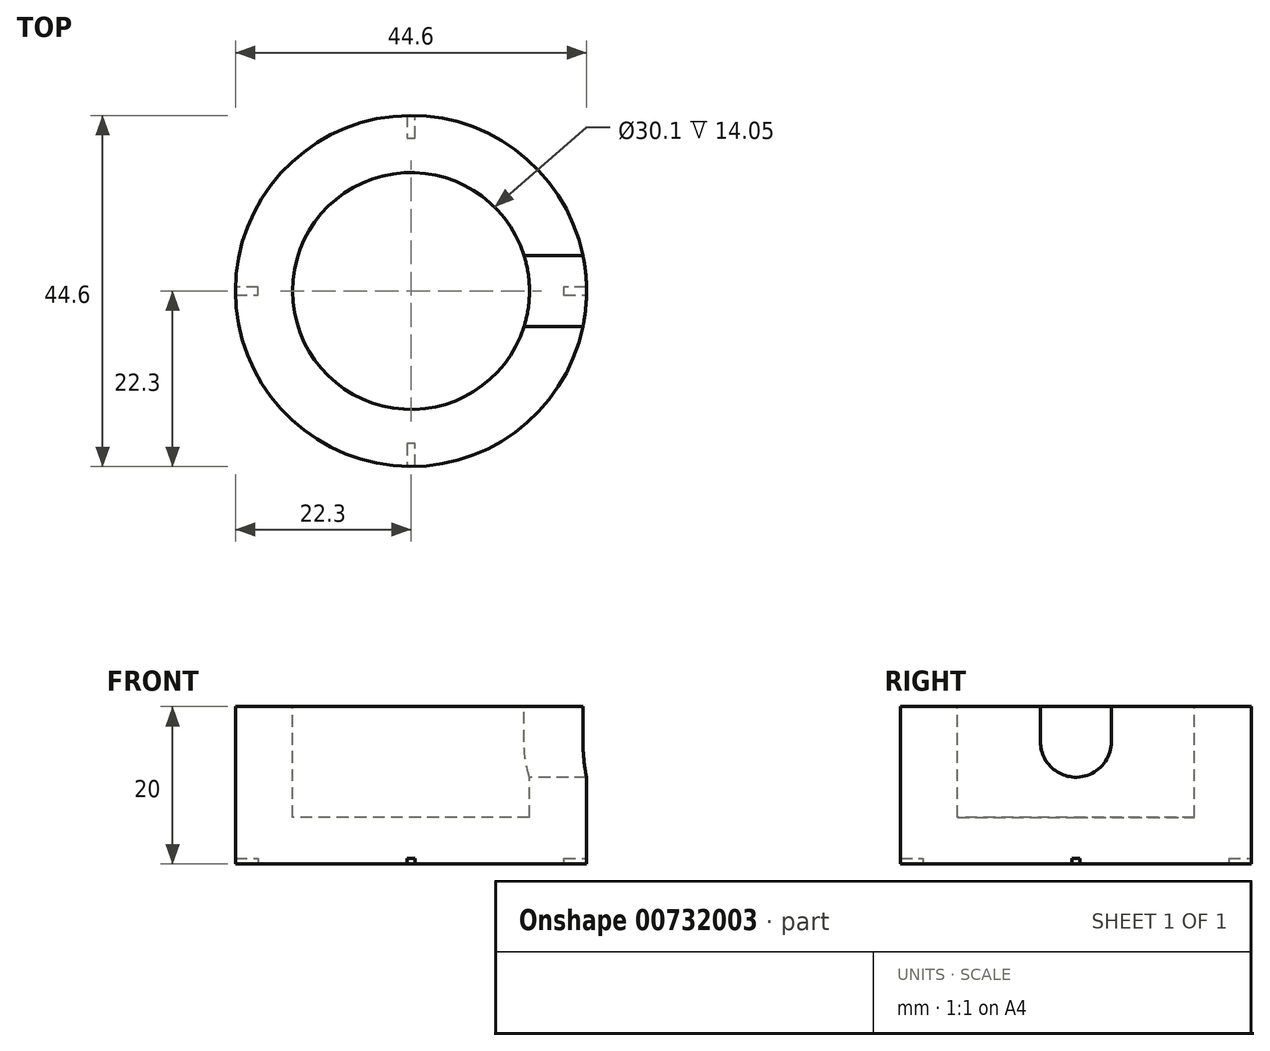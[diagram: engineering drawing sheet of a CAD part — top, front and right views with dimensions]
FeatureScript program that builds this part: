
annotation { "Feature Type Name" : "Feature", "Feature Type Description" : "" }
export const myFeature = defineFeature(function(context is Context, id is Id, definition is map)
    precondition{}
    {
        {
            var Q0;
            Q0=qCreatedBy(makeId("Front.planeOp"),FACE);
            var sketch = newSketch(context, id + "F0", { "sketchPlane" : qUnion([Q0])});
            skLineSegment(sketch, "E0", {"start": v(0, 0) * mm, "end": v(22.3, 0) * mm});
            skLineSegment(sketch, "E1", {"start": v(22.3, 0) * mm, "end": v(22.3, 20) * mm});
            skLineSegment(sketch, "E2", {"start": v(22.3, 20) * mm, "end": v(15.05, 20) * mm});
            skLineSegment(sketch, "E3", {"start": v(15.05, 20) * mm, "end": v(15.05, 5.95) * mm});
            skLineSegment(sketch, "E4", {"start": v(15.05, 5.95) * mm, "end": v(0, 5.95) * mm});
            skLineSegment(sketch, "E5", {"start": v(0, 5.95) * mm, "end": v(0, 0) * mm});
            skSolve(sketch);
        }
        {
            var Q0;
            Q0 = qSketchRegion(id + "F0", true);
            var Q1;
            Q1=sQuery(id+"F0.wireOp",EDGE,"E5");
            revolve(context, id + "F1", {"surfaceOperationType" : NewSurfaceOperationType.NEW, "entities" : qUnion([Q0]), "axis" : qUnion([Q1]), "revolveType" : RevolveType.FULL});
        }
        {
            var Q0;
            Q0=qCreatedBy(makeId("Right.planeOp"),FACE);
            var sketch = newSketch(context, id + "F2", { "sketchPlane" : qUnion([Q0])});
            skLineSegment(sketch, "E6", {"start": v(0, 20.02) * mm, "end": v(4.5, 20.02) * mm});
            skLineSegment(sketch, "E7", {"start": v(4.5, 20.02) * mm, "end": v(4.5, 15.52) * mm});
            skLineSegment(sketch, "E8", {"start": v(-4.5, 15.52) * mm, "end": v(-4.5, 20.02) * mm});
            skLineSegment(sketch, "E9", {"start": v(-4.5, 20.02) * mm, "end": v(0, 20.02) * mm});
            skArc(sketch, "E10", {"start": v(0, 11.04) * mm, "mid": v(-3.18, 12.35) * mm, "end": v(-4.5, 15.54) * mm});
            skPoint(sketch, "E10.startSnap0", {"position": v(0, 15.52) * mm});
            skArc(sketch, "E11", {"start": v(0, 11.04) * mm, "mid": v(3.18, 12.35) * mm, "end": v(4.5, 15.54) * mm});
            skSolve(sketch);
        }
        {
            var Q0;
            Q0=makeQuery(id+"F2.imprint","IMPRINT",FACE,{"disambiguationData":[TD([[makeQuery(id+"F2.imprint","IMPRINT",EDGE,{"derivedFrom":sQuery(id+"F2.wireOp",EDGE,"E6")}),-1.0]])]});
            extrude(context, id + "F3", {"entities" : qUnion([Q0]), "operationType" : NewBodyOperationType.REMOVE, "depth" : 25 * mm, "offsetDistance" : 25 * mm});
        }
        {
            var Q0;
            Q0=qCreatedBy(makeId("Top.planeOp"),FACE);
            var sketch = newSketch(context, id + "F4", { "sketchPlane" : qUnion([Q0])});
            skLineSegment(sketch, "E12", {"start": v(0, -19.4) * mm, "end": v(0.5, -19.4) * mm});
            skLineSegment(sketch, "E13", {"start": v(0.5, -19.4) * mm, "end": v(0.5, -22.4) * mm});
            skLineSegment(sketch, "E14", {"start": v(0.5, -22.4) * mm, "end": v(-0.5, -22.4) * mm});
            skLineSegment(sketch, "E15", {"start": v(-0.5, -22.4) * mm, "end": v(-0.5, -19.4) * mm});
            skLineSegment(sketch, "E16", {"start": v(-0.5, -19.4) * mm, "end": v(0, -19.4) * mm});
            skLineSegment(sketch, "E17", {"start": v(0, 22.42) * mm, "end": v(0.5, 22.42) * mm});
            skLineSegment(sketch, "E18", {"start": v(0.5, 22.42) * mm, "end": v(0.5, 19.42) * mm});
            skLineSegment(sketch, "E19", {"start": v(0.5, 19.42) * mm, "end": v(-0.5, 19.42) * mm});
            skLineSegment(sketch, "E20", {"start": v(-0.5, 19.42) * mm, "end": v(-0.5, 22.42) * mm});
            skLineSegment(sketch, "E21", {"start": v(-0.5, 22.42) * mm, "end": v(0, 22.42) * mm});
            skLineSegment(sketch, "E22", {"start": v(22.4, 0) * mm, "end": v(22.4, -0.5) * mm});
            skLineSegment(sketch, "E23", {"start": v(22.4, -0.5) * mm, "end": v(19.4, -0.5) * mm});
            skLineSegment(sketch, "E24", {"start": v(19.4, -0.5) * mm, "end": v(19.4, 0.5) * mm});
            skLineSegment(sketch, "E25", {"start": v(19.4, 0.5) * mm, "end": v(22.4, 0.5) * mm});
            skLineSegment(sketch, "E26", {"start": v(22.4, 0.5) * mm, "end": v(22.4, 0) * mm});
            skLineSegment(sketch, "E27", {"start": v(-19.4, 0) * mm, "end": v(-19.4, -0.5) * mm});
            skLineSegment(sketch, "E28", {"start": v(-19.4, -0.5) * mm, "end": v(-22.4, -0.5) * mm});
            skLineSegment(sketch, "E29", {"start": v(-22.4, -0.5) * mm, "end": v(-22.4, 0.5) * mm});
            skLineSegment(sketch, "E30", {"start": v(-22.4, 0.5) * mm, "end": v(-19.4, 0.5) * mm});
            skLineSegment(sketch, "E31", {"start": v(-19.4, 0.5) * mm, "end": v(-19.4, 0) * mm});
            skSolve(sketch);
        }
        {
            var Q0;
            Q0 = qSketchRegion(id + "F4", true);
            var Q1;
            Q1=sQuery(id+"F4.wireOp",EDGE,"E28");
            var Q2;
            Q2=sQuery(id+"F4.wireOp",EDGE,"E20");
            var Q3;
            Q3=sQuery(id+"F4.wireOp",EDGE,"E23");
            var Q4;
            Q4=sQuery(id+"F4.wireOp",EDGE,"E15");
            var Q5;
            Q5=sQuery(id+"F4.wireOp",EDGE,"E25");
            var Q6;
            Q6=sQuery(id+"F4.wireOp",EDGE,"E30");
            var Q7;
            Q7=sQuery(id+"F4.wireOp",EDGE,"E13");
            var Q8;
            Q8=sQuery(id+"F4.wireOp",EDGE,"E18");
            var Q9;
            Q9=sQuery(id+"F4.wireOp",EDGE,"E24");
            var Q10;
            Q10=sQuery(id+"F4.wireOp",EDGE,"E19");
            var Q11;
            Q11=sQuery(id+"F4.wireOp",EDGE,"E29");
            var Q12;
            Q12=sQuery(id+"F4.wireOp",EDGE,"E14");
            var Q13;
            Q13=sQuery(id+"F4.wireOp",EDGE,"E27");
            var Q14;
            Q14=sQuery(id+"F4.wireOp",EDGE,"E12");
            var Q15;
            Q15=sQuery(id+"F4.wireOp",EDGE,"E21");
            var Q16;
            Q16=sQuery(id+"F4.wireOp",EDGE,"E31");
            var Q17;
            Q17=sQuery(id+"F4.wireOp",EDGE,"E17");
            var Q18;
            Q18=sQuery(id+"F4.wireOp",EDGE,"E16");
            var Q19;
            Q19=sQuery(id+"F4.wireOp",EDGE,"E26");
            var Q20;
            Q20=sQuery(id+"F4.wireOp",EDGE,"E22");
            extrude(context, id + "F5", {"entities" : qUnion([Q0]), "operationType" : NewBodyOperationType.REMOVE, "surfaceEntities" : qUnion([Q1, Q2, Q3, Q4, Q5, Q6, Q7, Q8, Q9, Q10, Q11, Q12, Q13, Q14, Q15, Q16, Q17, Q18, Q19, Q20]), "depth" : 1.5 * mm, "offsetDistance" : 25 * mm, "symmetric" : true});
        }
    });
